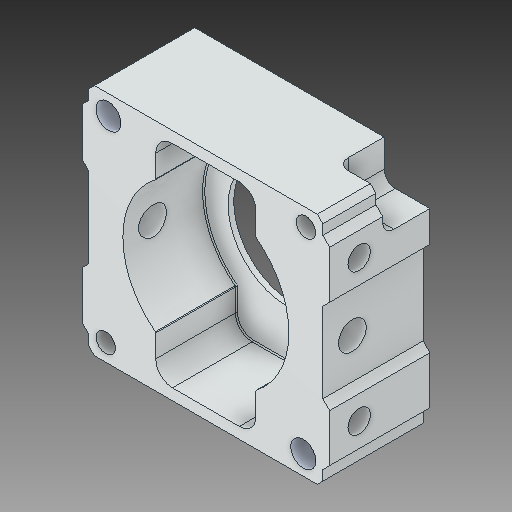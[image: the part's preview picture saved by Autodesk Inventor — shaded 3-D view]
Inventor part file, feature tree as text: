
AUTODESK INVENTOR PART (.ipt)
format: ipt  version: 2017 (Build 210142000, 142)  size: 266,752 bytes
history: native  units: in
note: dims shown in document units (in); Inventor stores cm internally (conversion verified against a paired STEP export)
features: chamfer x1
ambient origin geometry x8: Origin, YZ Plane, XZ Plane, XY Plane, X Axis, Y Axis, Z Axis, Center Point
bodies: Solid1 (feature_tree)
feature tree (1):
  chamfer  "Chamfer4"  [1 undecoded]
note: 1 required parameter value undecoded (feature->parameter linkage not recoverable at this tier; creation-order binding heuristic only, values carry confidence <= 0.55)
